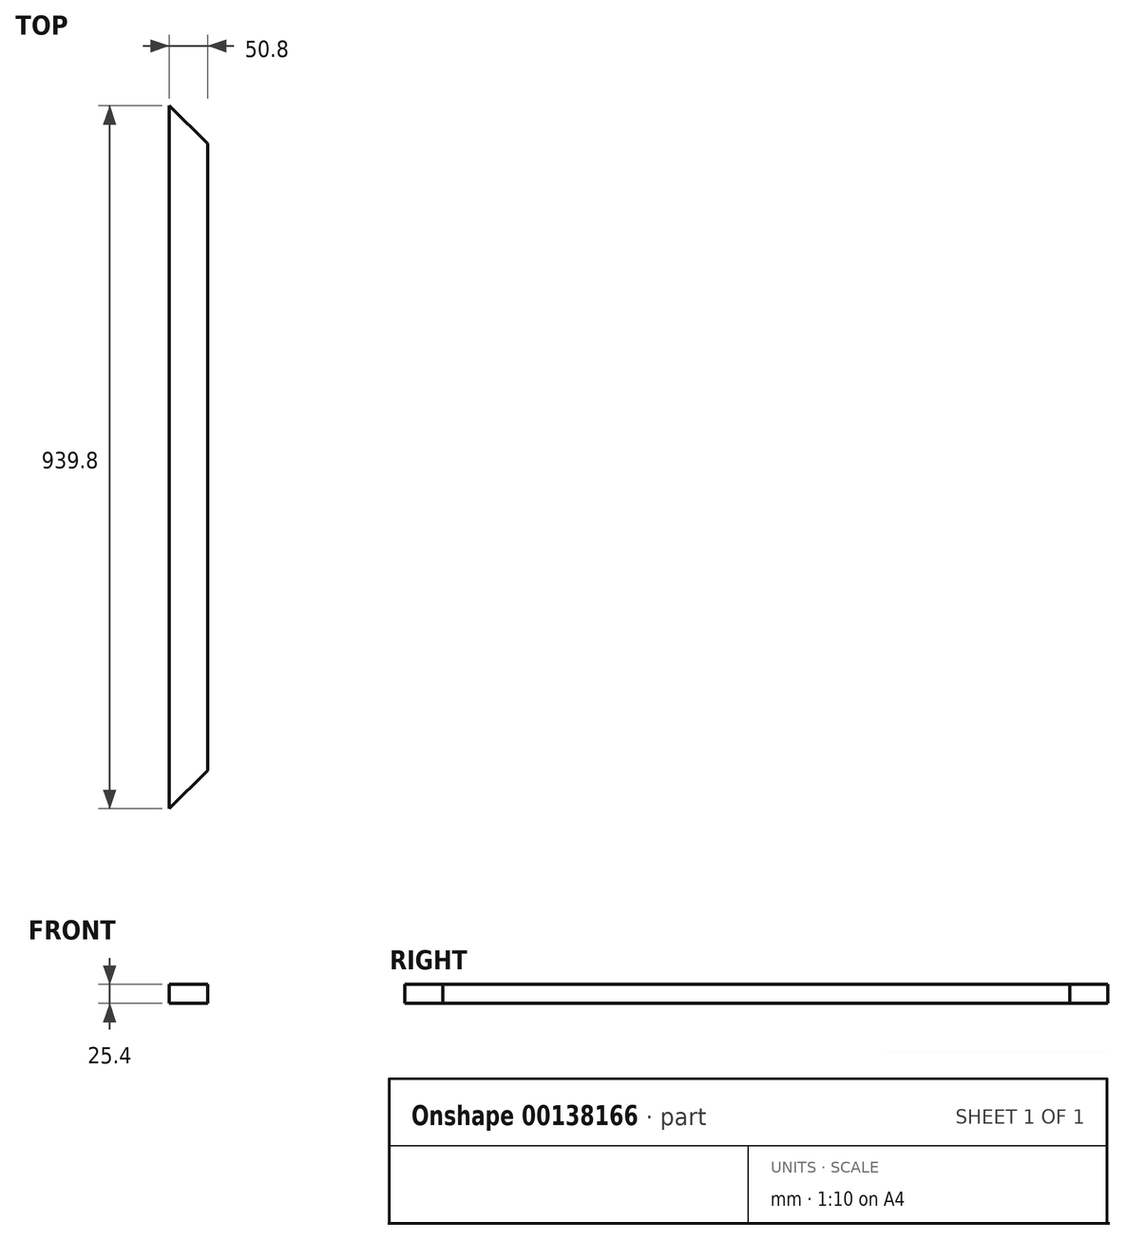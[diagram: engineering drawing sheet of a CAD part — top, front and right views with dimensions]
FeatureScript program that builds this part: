
annotation { "Feature Type Name" : "Feature", "Feature Type Description" : "" }
export const myFeature = defineFeature(function(context is Context, id is Id, definition is map)
    precondition{}
    {
        {
            var Q0;
            Q0=qCreatedBy(makeId("Top.planeOp"),FACE);
            var sketch = newSketch(context, id + "F0", { "sketchPlane" : qUnion([Q0])});
            skLineSegment(sketch, "E0", {"start": v(-78.42, 469.33) * mm, "end": v(-78.42, -470.47) * mm});
            skLineSegment(sketch, "E1", {"start": v(-78.42, -470.47) * mm, "end": v(-27.62, -419.67) * mm});
            skLineSegment(sketch, "E2", {"start": v(-27.62, -419.67) * mm, "end": v(-27.62, 418.53) * mm});
            skLineSegment(sketch, "E3", {"start": v(-27.62, 418.53) * mm, "end": v(-78.42, 469.33) * mm});
            skSolve(sketch);
        }
        {
            var Q0;
            Q0=makeQuery(id+"F0.imprint","IMPRINT",FACE,{"disambiguationData":[TD([[makeQuery(id+"F0.imprint","IMPRINT",EDGE,{"derivedFrom":sQuery(id+"F0.wireOp",EDGE,"E0")}),1.0]])]});
            extrude(context, id + "F1", {"entities" : qUnion([Q0]), "depth" : 25.4 * mm});
        }
    });
